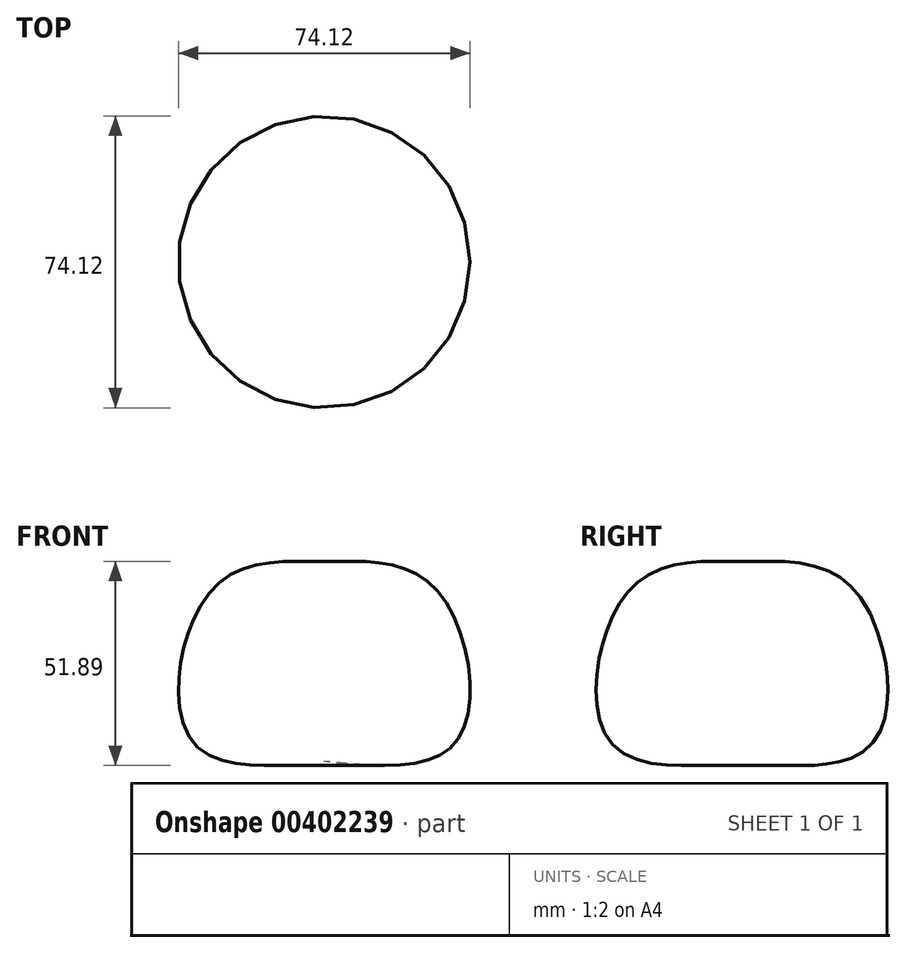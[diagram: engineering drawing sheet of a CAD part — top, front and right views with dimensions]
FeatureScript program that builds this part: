
annotation { "Feature Type Name" : "Feature", "Feature Type Description" : "" }
export const myFeature = defineFeature(function(context is Context, id is Id, definition is map)
    precondition{}
    {
        {
            var Q0;
            Q0=qCreatedBy(makeId("Front.planeOp"),FACE);
            var sketch = newSketch(context, id + "F0", { "sketchPlane" : qUnion([Q0])});
            skLineSegment(sketch, "E0", {"start": v(0, 0) * mm, "end": v(0, -50.72) * mm});
            skFitSpline(sketch, "E1", {"points": [v(0, 0) * mm, v(28.53, -7.12) * mm, v(34.02, -44.92) * mm, v(0, -50.72) * mm], "startDerivative": vector(103.63, 3.87) * mm, "endDerivative": vector(-126.4, 12.04) * mm});
            skSolve(sketch);
        }
        {
            var Q0;
            Q0=makeQuery(id+"F0.imprint","IMPRINT",FACE,{"disambiguationData":[TD([[makeQuery(id+"F0.imprint","IMPRINT",EDGE,{"derivedFrom":sQuery(id+"F0.wireOp",EDGE,"E0")}),1.0]])]});
            var Q1;
            Q1=sQuery(id+"F0.wireOp",EDGE,"E0");
            revolve(context, id + "F1", {"entities" : qUnion([Q0]), "axis" : qUnion([Q1]), "revolveType" : RevolveType.FULL});
        }
    });
